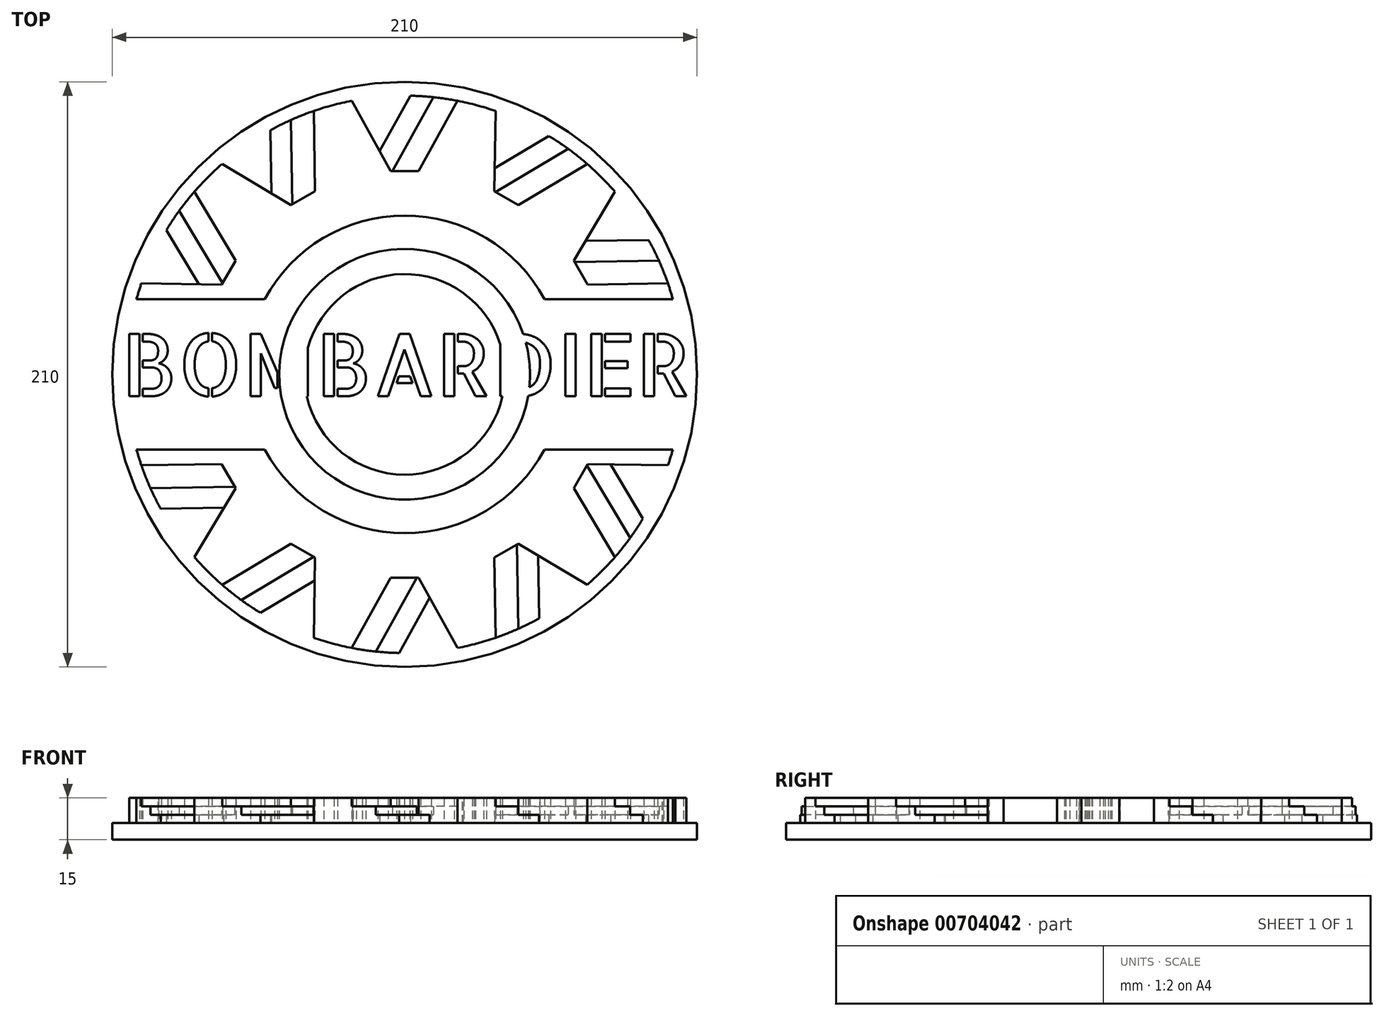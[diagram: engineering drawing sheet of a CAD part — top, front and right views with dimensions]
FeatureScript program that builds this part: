
annotation { "Feature Type Name" : "Feature", "Feature Type Description" : "" }
export const myFeature = defineFeature(function(context is Context, id is Id, definition is map)
    precondition{}
    {
        {
            var Q0;
            Q0=qCreatedBy(makeId("Top.planeOp"),FACE);
            var sketch = newSketch(context, id + "F0", { "sketchPlane" : qUnion([Q0])});
            skCircle(sketch, "E0", {"center": v(0, 0) * mm, "radius": 105 * mm});
            skSolve(sketch);
        }
        {
            var Q0;
            Q0=makeQuery(id+"F0.imprint","IMPRINT",FACE,{"disambiguationData":[TD([[makeQuery(id+"F0.imprint","IMPRINT",EDGE,{"derivedFrom":sQuery(id+"F0.wireOp",EDGE,"E0")}),1.0]])]});
            extrude(context, id + "F1", {"entities" : qUnion([Q0]), "depth" : 6 * mm, "offsetDistance" : 25 * mm});
        }
        {
            var Q0;
            Q0=makeQuery(id+"F1.opExtrude","CAP_FACE",FACE,{"disambiguationData":[OSD([sQuery(id+"F0.wireOp",EDGE,"E0")])],"isStart":false});
            var sketch = newSketch(context, id + "F2", { "sketchPlane" : qUnion([Q0])});
            skCircle(sketch, "E1", {"center": v(0, 0) * mm, "radius": 100 * mm});
            skCircle(sketch, "E2", {"center": v(0, 0) * mm, "radius": 57 * mm});
            skLineSegment(sketch, "E3", {"start": v(0, 98.18) * mm, "end": v(-19, 98.18) * mm});
            skLineSegment(sketch, "E4", {"start": v(-19, 98.18) * mm, "end": v(-5, 73) * mm});
            skLineSegment(sketch, "E5", {"start": v(-5, 73) * mm, "end": v(0, 73) * mm});
            skLineSegment(sketch, "E6.MirrorCS", {"start": v(5, 73) * mm, "end": v(0, 73) * mm});
            skLineSegment(sketch, "E7.MirrorCS", {"start": v(19, 98.18) * mm, "end": v(5, 73) * mm});
            skLineSegment(sketch, "E8.MirrorCS", {"start": v(0, 98.18) * mm, "end": v(19, 98.18) * mm});
            skLineSegment(sketch, "E9.1.0", {"start": v(-49.09, 85.02) * mm, "end": v(-65.54, 75.52) * mm});
            skLineSegment(sketch, "E9.1.1", {"start": v(-49.09, 85.02) * mm, "end": v(-32.63, 94.52) * mm});
            skLineSegment(sketch, "E9.1.2", {"start": v(-32.63, 94.52) * mm, "end": v(-32.17, 65.72) * mm});
            skLineSegment(sketch, "E9.1.3", {"start": v(-32.17, 65.72) * mm, "end": v(-36.5, 63.22) * mm});
            skLineSegment(sketch, "E9.1.4", {"start": v(-40.83, 60.72) * mm, "end": v(-36.5, 63.22) * mm});
            skLineSegment(sketch, "E9.1.5", {"start": v(-65.54, 75.52) * mm, "end": v(-40.83, 60.72) * mm});
            skLineSegment(sketch, "E9.2.0", {"start": v(-85.02, 49.09) * mm, "end": v(-94.52, 32.63) * mm});
            skLineSegment(sketch, "E9.2.1", {"start": v(-85.02, 49.09) * mm, "end": v(-75.52, 65.54) * mm});
            skLineSegment(sketch, "E9.2.2", {"start": v(-75.52, 65.54) * mm, "end": v(-60.72, 40.83) * mm});
            skLineSegment(sketch, "E9.2.3", {"start": v(-60.72, 40.83) * mm, "end": v(-63.22, 36.5) * mm});
            skLineSegment(sketch, "E9.2.4", {"start": v(-65.72, 32.17) * mm, "end": v(-63.22, 36.5) * mm});
            skLineSegment(sketch, "E9.2.5", {"start": v(-94.52, 32.63) * mm, "end": v(-65.72, 32.17) * mm});
            skLineSegment(sketch, "E9.3.0", {"start": v(-98.18, 0) * mm, "end": v(-98.18, -19) * mm});
            skLineSegment(sketch, "E9.3.1", {"start": v(-98.18, 0) * mm, "end": v(-98.18, 19) * mm});
            skLineSegment(sketch, "E9.3.2", {"start": v(-98.18, 19) * mm, "end": v(-73, 5) * mm});
            skLineSegment(sketch, "E9.3.3", {"start": v(-73, 5) * mm, "end": v(-73, 0) * mm});
            skLineSegment(sketch, "E9.3.4", {"start": v(-73, -5) * mm, "end": v(-73, 0) * mm});
            skLineSegment(sketch, "E9.3.5", {"start": v(-98.18, -19) * mm, "end": v(-73, -5) * mm});
            skLineSegment(sketch, "E9.4.0", {"start": v(-85.02, -49.09) * mm, "end": v(-75.52, -65.54) * mm});
            skLineSegment(sketch, "E9.4.1", {"start": v(-85.02, -49.09) * mm, "end": v(-94.52, -32.63) * mm});
            skLineSegment(sketch, "E9.4.2", {"start": v(-94.52, -32.63) * mm, "end": v(-65.72, -32.17) * mm});
            skLineSegment(sketch, "E9.4.3", {"start": v(-65.72, -32.17) * mm, "end": v(-63.22, -36.5) * mm});
            skLineSegment(sketch, "E9.4.4", {"start": v(-60.72, -40.83) * mm, "end": v(-63.22, -36.5) * mm});
            skLineSegment(sketch, "E9.4.5", {"start": v(-75.52, -65.54) * mm, "end": v(-60.72, -40.83) * mm});
            skLineSegment(sketch, "E9.5.0", {"start": v(-49.09, -85.02) * mm, "end": v(-32.63, -94.52) * mm});
            skLineSegment(sketch, "E9.5.1", {"start": v(-49.09, -85.02) * mm, "end": v(-65.54, -75.52) * mm});
            skLineSegment(sketch, "E9.5.2", {"start": v(-65.54, -75.52) * mm, "end": v(-40.83, -60.72) * mm});
            skLineSegment(sketch, "E9.5.3", {"start": v(-40.83, -60.72) * mm, "end": v(-36.5, -63.22) * mm});
            skLineSegment(sketch, "E9.5.4", {"start": v(-32.17, -65.72) * mm, "end": v(-36.5, -63.22) * mm});
            skLineSegment(sketch, "E9.5.5", {"start": v(-32.63, -94.52) * mm, "end": v(-32.17, -65.72) * mm});
            skLineSegment(sketch, "E9.6.0", {"start": v(0, -98.18) * mm, "end": v(19, -98.18) * mm});
            skLineSegment(sketch, "E9.6.1", {"start": v(0, -98.18) * mm, "end": v(-19, -98.18) * mm});
            skLineSegment(sketch, "E9.6.2", {"start": v(-19, -98.18) * mm, "end": v(-5, -73) * mm});
            skLineSegment(sketch, "E9.6.3", {"start": v(-5, -73) * mm, "end": v(0, -73) * mm});
            skLineSegment(sketch, "E9.6.4", {"start": v(5, -73) * mm, "end": v(0, -73) * mm});
            skLineSegment(sketch, "E9.6.5", {"start": v(19, -98.18) * mm, "end": v(5, -73) * mm});
            skLineSegment(sketch, "E9.7.0", {"start": v(49.09, -85.02) * mm, "end": v(65.54, -75.52) * mm});
            skLineSegment(sketch, "E9.7.1", {"start": v(49.09, -85.02) * mm, "end": v(32.63, -94.52) * mm});
            skLineSegment(sketch, "E9.7.2", {"start": v(32.63, -94.52) * mm, "end": v(32.17, -65.72) * mm});
            skLineSegment(sketch, "E9.7.3", {"start": v(32.17, -65.72) * mm, "end": v(36.5, -63.22) * mm});
            skLineSegment(sketch, "E9.7.4", {"start": v(40.83, -60.72) * mm, "end": v(36.5, -63.22) * mm});
            skLineSegment(sketch, "E9.7.5", {"start": v(65.54, -75.52) * mm, "end": v(40.83, -60.72) * mm});
            skLineSegment(sketch, "E9.8.0", {"start": v(85.02, -49.09) * mm, "end": v(94.52, -32.63) * mm});
            skLineSegment(sketch, "E9.8.1", {"start": v(85.02, -49.09) * mm, "end": v(75.52, -65.54) * mm});
            skLineSegment(sketch, "E9.8.2", {"start": v(75.52, -65.54) * mm, "end": v(60.72, -40.83) * mm});
            skLineSegment(sketch, "E9.8.3", {"start": v(60.72, -40.83) * mm, "end": v(63.22, -36.5) * mm});
            skLineSegment(sketch, "E9.8.4", {"start": v(65.72, -32.17) * mm, "end": v(63.22, -36.5) * mm});
            skLineSegment(sketch, "E9.8.5", {"start": v(94.52, -32.63) * mm, "end": v(65.72, -32.17) * mm});
            skLineSegment(sketch, "E9.9.0", {"start": v(98.18, 0) * mm, "end": v(98.18, 19) * mm});
            skLineSegment(sketch, "E9.9.1", {"start": v(98.18, 0) * mm, "end": v(98.18, -19) * mm});
            skLineSegment(sketch, "E9.9.2", {"start": v(98.18, -19) * mm, "end": v(73, -5) * mm});
            skLineSegment(sketch, "E9.9.3", {"start": v(73, -5) * mm, "end": v(73, 0) * mm});
            skLineSegment(sketch, "E9.9.4", {"start": v(73, 5) * mm, "end": v(73, 0) * mm});
            skLineSegment(sketch, "E9.9.5", {"start": v(98.18, 19) * mm, "end": v(73, 5) * mm});
            skLineSegment(sketch, "E9.10.0", {"start": v(85.02, 49.09) * mm, "end": v(75.52, 65.54) * mm});
            skLineSegment(sketch, "E9.10.1", {"start": v(85.02, 49.09) * mm, "end": v(94.52, 32.63) * mm});
            skLineSegment(sketch, "E9.10.2", {"start": v(94.52, 32.63) * mm, "end": v(65.72, 32.17) * mm});
            skLineSegment(sketch, "E9.10.3", {"start": v(65.72, 32.17) * mm, "end": v(63.22, 36.5) * mm});
            skLineSegment(sketch, "E9.10.4", {"start": v(60.72, 40.83) * mm, "end": v(63.22, 36.5) * mm});
            skLineSegment(sketch, "E9.10.5", {"start": v(75.52, 65.54) * mm, "end": v(60.72, 40.83) * mm});
            skLineSegment(sketch, "E9.11.0", {"start": v(49.09, 85.02) * mm, "end": v(32.63, 94.52) * mm});
            skLineSegment(sketch, "E9.11.1", {"start": v(49.09, 85.02) * mm, "end": v(65.54, 75.52) * mm});
            skLineSegment(sketch, "E9.11.2", {"start": v(65.54, 75.52) * mm, "end": v(40.83, 60.72) * mm});
            skLineSegment(sketch, "E9.11.3", {"start": v(40.83, 60.72) * mm, "end": v(36.5, 63.22) * mm});
            skLineSegment(sketch, "E9.11.4", {"start": v(32.17, 65.72) * mm, "end": v(36.5, 63.22) * mm});
            skLineSegment(sketch, "E9.11.5", {"start": v(32.63, 94.52) * mm, "end": v(32.17, 65.72) * mm});
            skCircle(sketch, "E10", {"center": v(0, 0) * mm, "radius": 45 * mm});
            skCircle(sketch, "E11", {"center": v(0, 0) * mm, "radius": 36 * mm});
            skLineSegment(sketch, "E12", {"start": v(13, 99.15) * mm, "end": v(-1.54, 73) * mm});
            skLineSegment(sketch, "E13", {"start": v(-4.4, 73) * mm, "end": v(10.31, 99.47) * mm});
            skLineSegment(sketch, "E14", {"start": v(4.83, 99.88) * mm, "end": v(-7.56, 77.6) * mm});
            skLineSegment(sketch, "E15", {"start": v(2.02, 99.98) * mm, "end": v(-9, 80.18) * mm});
            skLineSegment(sketch, "E16.1.0", {"start": v(-38.32, 92.37) * mm, "end": v(-37.83, 62.45) * mm});
            skLineSegment(sketch, "E16.1.1", {"start": v(-40.31, 61.02) * mm, "end": v(-40.8, 91.3) * mm});
            skLineSegment(sketch, "E16.1.2", {"start": v(-45.76, 88.91) * mm, "end": v(-45.35, 63.43) * mm});
            skLineSegment(sketch, "E16.1.3", {"start": v(-48.24, 87.6) * mm, "end": v(-47.88, 64.94) * mm});
            skLineSegment(sketch, "E16.2.0", {"start": v(-79.37, 60.83) * mm, "end": v(-64, 35.17) * mm});
            skLineSegment(sketch, "E16.2.1", {"start": v(-65.42, 32.69) * mm, "end": v(-80.98, 58.67) * mm});
            skLineSegment(sketch, "E16.2.2", {"start": v(-84.09, 54.12) * mm, "end": v(-70.99, 32.25) * mm});
            skLineSegment(sketch, "E16.2.3", {"start": v(-85.58, 51.74) * mm, "end": v(-73.93, 32.3) * mm});
            skLineSegment(sketch, "E16.3.0", {"start": v(-99.15, 13) * mm, "end": v(-73, -1.54) * mm});
            skLineSegment(sketch, "E16.3.1", {"start": v(-73, -4.4) * mm, "end": v(-99.47, 10.31) * mm});
            skLineSegment(sketch, "E16.3.2", {"start": v(-99.88, 4.83) * mm, "end": v(-77.6, -7.56) * mm});
            skLineSegment(sketch, "E16.3.3", {"start": v(-99.98, 2.02) * mm, "end": v(-80.18, -9) * mm});
            skLineSegment(sketch, "E16.4.0", {"start": v(-92.37, -38.32) * mm, "end": v(-62.45, -37.83) * mm});
            skLineSegment(sketch, "E16.4.1", {"start": v(-61.02, -40.31) * mm, "end": v(-91.3, -40.8) * mm});
            skLineSegment(sketch, "E16.4.2", {"start": v(-88.91, -45.76) * mm, "end": v(-63.43, -45.35) * mm});
            skLineSegment(sketch, "E16.4.3", {"start": v(-87.6, -48.24) * mm, "end": v(-64.94, -47.88) * mm});
            skLineSegment(sketch, "E16.5.0", {"start": v(-60.83, -79.37) * mm, "end": v(-35.17, -64) * mm});
            skLineSegment(sketch, "E16.5.1", {"start": v(-32.69, -65.42) * mm, "end": v(-58.67, -80.98) * mm});
            skLineSegment(sketch, "E16.5.2", {"start": v(-54.12, -84.09) * mm, "end": v(-32.25, -70.99) * mm});
            skLineSegment(sketch, "E16.5.3", {"start": v(-51.74, -85.58) * mm, "end": v(-32.3, -73.93) * mm});
            skLineSegment(sketch, "E16.6.0", {"start": v(-13, -99.15) * mm, "end": v(1.54, -73) * mm});
            skLineSegment(sketch, "E16.6.1", {"start": v(4.4, -73) * mm, "end": v(-10.31, -99.47) * mm});
            skLineSegment(sketch, "E16.6.2", {"start": v(-4.83, -99.88) * mm, "end": v(7.56, -77.6) * mm});
            skLineSegment(sketch, "E16.6.3", {"start": v(-2.02, -99.98) * mm, "end": v(9, -80.18) * mm});
            skLineSegment(sketch, "E16.7.0", {"start": v(38.32, -92.37) * mm, "end": v(37.83, -62.45) * mm});
            skLineSegment(sketch, "E16.7.1", {"start": v(40.31, -61.02) * mm, "end": v(40.8, -91.3) * mm});
            skLineSegment(sketch, "E16.7.2", {"start": v(45.76, -88.91) * mm, "end": v(45.35, -63.43) * mm});
            skLineSegment(sketch, "E16.7.3", {"start": v(48.24, -87.6) * mm, "end": v(47.88, -64.94) * mm});
            skLineSegment(sketch, "E16.8.0", {"start": v(79.37, -60.83) * mm, "end": v(64, -35.17) * mm});
            skLineSegment(sketch, "E16.8.1", {"start": v(65.42, -32.69) * mm, "end": v(80.98, -58.67) * mm});
            skLineSegment(sketch, "E16.8.2", {"start": v(84.09, -54.12) * mm, "end": v(70.99, -32.25) * mm});
            skLineSegment(sketch, "E16.8.3", {"start": v(85.58, -51.74) * mm, "end": v(73.93, -32.3) * mm});
            skLineSegment(sketch, "E16.9.0", {"start": v(99.15, -13) * mm, "end": v(73, 1.54) * mm});
            skLineSegment(sketch, "E16.9.1", {"start": v(73, 4.4) * mm, "end": v(99.47, -10.31) * mm});
            skLineSegment(sketch, "E16.9.2", {"start": v(99.88, -4.83) * mm, "end": v(77.6, 7.56) * mm});
            skLineSegment(sketch, "E16.9.3", {"start": v(99.98, -2.02) * mm, "end": v(80.18, 9) * mm});
            skLineSegment(sketch, "E16.10.0", {"start": v(92.37, 38.32) * mm, "end": v(62.45, 37.83) * mm});
            skLineSegment(sketch, "E16.10.1", {"start": v(61.02, 40.31) * mm, "end": v(91.3, 40.8) * mm});
            skLineSegment(sketch, "E16.10.2", {"start": v(88.91, 45.76) * mm, "end": v(63.43, 45.35) * mm});
            skLineSegment(sketch, "E16.10.3", {"start": v(87.6, 48.24) * mm, "end": v(64.94, 47.88) * mm});
            skLineSegment(sketch, "E16.11.0", {"start": v(60.83, 79.37) * mm, "end": v(35.17, 64) * mm});
            skLineSegment(sketch, "E16.11.1", {"start": v(32.69, 65.42) * mm, "end": v(58.67, 80.98) * mm});
            skLineSegment(sketch, "E16.11.2", {"start": v(54.12, 84.09) * mm, "end": v(32.25, 70.99) * mm});
            skLineSegment(sketch, "E16.11.3", {"start": v(51.74, 85.58) * mm, "end": v(32.3, 73.93) * mm});
            skSolve(sketch);
        }
        {
            var Q0;
            Q0=makeQuery(id+"F2.imprint","IMPRINT",FACE,{"disambiguationData":[TD([[makeQuery(id+"F2.imprint","IMPRINT",EDGE,{"derivedFrom":sQuery(id+"F2.wireOp",EDGE,"E2")}),-1.0]])]});
            var Q1;
            Q1=makeQuery(id+"F2.imprint","IMPRINT",FACE,{"disambiguationData":[TD([[makeQuery(id+"F2.imprint","IMPRINT",EDGE,{"derivedFrom":sQuery(id+"F2.wireOp",EDGE,"E10")}),1.0]])]});
            extrude(context, id + "F3", {"entities" : qUnion([Q0, Q1]), "operationType" : NewBodyOperationType.ADD, "depth" : 9 * mm, "offsetDistance" : 25 * mm});
        }
        {
            var Q0;
            Q0=makeQuery(id+"F3.boolean.opBoolean","SPLIT",FACE,{"disambiguationData":[TD([makeQuery(id+"F3.opExtrude","SWEPT_FACE",FACE,{"disambiguationData":[OSD([sQuery(id+"F2.wireOp",EDGE,"E2")])]})])],"derivedFrom":makeQuery(id+"F1.opExtrude","CAP_FACE",FACE,{"disambiguationData":[OSD([sQuery(id+"F0.wireOp",EDGE,"E0")])],"isStart":false})});
            var sketch = newSketch(context, id + "F4", { "sketchPlane" : qUnion([Q0])});
            skLineSegment(sketch, "E17.bottom", {"start": v(-113.63, 27) * mm, "end": v(113.63, 27) * mm});
            skLineSegment(sketch, "E17.top", {"start": v(-113.63, -27) * mm, "end": v(113.63, -27) * mm});
            skLineSegment(sketch, "E17.left", {"start": v(-113.63, 27) * mm, "end": v(-113.63, -27) * mm});
            skLineSegment(sketch, "E17.right", {"start": v(113.63, 27) * mm, "end": v(113.63, -27) * mm});
            skPoint(sketch, "E17.middle", {"position": v(0, 0) * mm});
            skSolve(sketch);
        }
        {
            var Q0;
            {var subQ0=sQuery(id+"F4.wireOp",EDGE,"E17.left");Q0=makeQuery(id+"F4.imprint","IMPRINT",FACE,{"disambiguationData":[TD([[makeQuery(id+"F4.imprint","IMPRINT",EDGE,{"derivedFrom":subQ0}),1.0]])]});}
            var Q1;
            {var subQ0=sQuery(id+"F4.wireOp",EDGE,"E17.bottom");var subQ1=makeQuery(id+"F3.opExtrude","CAP_EDGE",EDGE,{"disambiguationData":[OSD([sQuery(id+"F2.wireOp",EDGE,"E10")])],"isStart":true});var subQ2=makeQuery(id+"F4.imprint","INTERSECT",VERTEX,{"disambiguationData":[OD(0.0)],"derivedFrom":[subQ1,subQ0]});Q1=makeQuery(id+"F4.imprint","IMPRINT",FACE,{"disambiguationData":[TD([[makeQuery(id+"F4.imprint","IMPRINT",EDGE,{"disambiguationData":[TD([[subQ2,-1.0]])],"derivedFrom":subQ0}),-1.0]])]});}
            var Q2;
            {var subQ0=sQuery(id+"F4.wireOp",EDGE,"E17.right");Q2=makeQuery(id+"F4.imprint","IMPRINT",FACE,{"disambiguationData":[TD([[makeQuery(id+"F4.imprint","IMPRINT",EDGE,{"derivedFrom":subQ0}),-1.0]])]});}
            extrude(context, id + "F5", {"entities" : qUnion([Q0, Q1, Q2]), "operationType" : NewBodyOperationType.REMOVE, "depth" : 52.9 * mm, "offsetDistance" : 25 * mm});
        }
        {
            var Q0;
            {var subQ0=sQuery(id+"F4.wireOp",EDGE,"E17.top");var subQ1=sQuery(id+"F4.wireOp",EDGE,"E17.bottom");var subQ2=sQuery(id+"F2.wireOp",EDGE,"E2");var subQ3=sQuery(id+"F2.wireOp",EDGE,"E10");var subQ4=sQuery(id+"F0.wireOp",EDGE,"E0");var subQ5=makeQuery(id+"F1.opExtrude","CAP_FACE",FACE,{"disambiguationData":[OSD([subQ4])],"isStart":false});Q0=makeQuery(id+"F5.boolean.opBoolean","MERGE",FACE,{"derivedFrom":[makeQuery(id+"F3.boolean.opBoolean","SPLIT",FACE,{"disambiguationData":[TD([makeQuery(id+"F1.opExtrude","SWEPT_FACE",FACE,{"disambiguationData":[OSD([subQ4])]})])],"derivedFrom":subQ5}),makeQuery(id+"F3.boolean.opBoolean","SPLIT",FACE,{"disambiguationData":[TD([makeQuery(id+"F3.opExtrude","SWEPT_FACE",FACE,{"disambiguationData":[OSD([subQ2])]})])],"derivedFrom":subQ5}),makeQuery(id+"F3.boolean.opBoolean","SPLIT",FACE,{"disambiguationData":[TD([makeQuery(id+"F3.opExtrude","SWEPT_FACE",FACE,{"disambiguationData":[OSD([sQuery(id+"F2.wireOp",EDGE,"E11")])]})])],"derivedFrom":subQ5}),makeQuery(id+"F5.opExtrude","CAP_FACE",FACE,{"disambiguationData":[OSD([subQ2,subQ1,subQ0,sQuery(id+"F4.wireOp",EDGE,"E17.left")])],"isStart":true}),makeQuery(id+"F5.opExtrude","CAP_FACE",FACE,{"disambiguationData":[OSD([subQ3,subQ1,subQ0])],"isStart":true}),makeQuery(id+"F5.opExtrude","CAP_FACE",FACE,{"disambiguationData":[OSD([subQ2,subQ1,subQ0,sQuery(id+"F4.wireOp",EDGE,"E17.right")])],"isStart":true})]});}
            var sketch = newSketch(context, id + "F6", { "sketchPlane" : qUnion([Q0])});
            skText(sketch, "E18", { "text": "BOMBARDIER", "fontName": "AllertaStencil-Regular.ttf"});
            const initialGuessF6  = {"E18": [-0.1018, -0.00782, 1, 0, 0.02236]};
            skSetInitialGuess(sketch, initialGuessF6);
            skSolve(sketch);
        }
        {
            var Q0;
            Q0 = qSketchRegion(id + "F6", true);
            extrude(context, id + "F7", {"entities" : qUnion([Q0]), "operationType" : NewBodyOperationType.ADD, "depth" : 9 * mm, "offsetDistance" : 25 * mm});
        }
        {
            var Q0;
            {var subQ0=sQuery(id+"F2.wireOp",EDGE,"E14");var subQ1=sQuery(id+"F2.wireOp",EDGE,"E1");var subQ2=makeQuery(id+"F2.imprint","INTERSECT",VERTEX,{"derivedFrom":[subQ1,subQ0]});Q0=makeQuery(id+"F2.imprint","IMPRINT",FACE,{"disambiguationData":[TD([[makeQuery(id+"F2.imprint","IMPRINT",EDGE,{"disambiguationData":[TD([[subQ2,-1.0]])],"derivedFrom":subQ1}),1.0]])]});}
            var Q1;
            {var subQ0=sQuery(id+"F2.wireOp",EDGE,"E14");var subQ1=sQuery(id+"F2.wireOp",EDGE,"E4");var subQ2=makeQuery(id+"F2.imprint","INTERSECT",VERTEX,{"derivedFrom":[subQ1,subQ0]});Q1=makeQuery(id+"F2.imprint","IMPRINT",FACE,{"disambiguationData":[TD([[makeQuery(id+"F2.imprint","IMPRINT",EDGE,{"disambiguationData":[TD([[subQ2,1.0]])],"derivedFrom":subQ1}),1.0]])]});}
            var Q2;
            {var subQ1=sQuery(id+"F2.wireOp",EDGE,"E5");var subQ7=sQuery(id+"F2.wireOp",EDGE,"E4");var subQ8=makeQuery(id+"F2.imprint","INTERSECT",VERTEX,{"derivedFrom":[subQ7,subQ1]});Q2=makeQuery(id+"F2.imprint","IMPRINT",FACE,{"disambiguationData":[TD([[makeQuery(id+"F2.imprint","IMPRINT",EDGE,{"disambiguationData":[TD([[subQ8,1.0]])],"derivedFrom":subQ7}),1.0]])]});}
            var Q3;
            {var subQ0=sQuery(id+"F2.wireOp",EDGE,"E13");var subQ1=sQuery(id+"F2.wireOp",EDGE,"E1");var subQ2=makeQuery(id+"F2.imprint","INTERSECT",VERTEX,{"derivedFrom":[subQ1,subQ0]});Q3=makeQuery(id+"F2.imprint","IMPRINT",FACE,{"disambiguationData":[TD([[makeQuery(id+"F2.imprint","IMPRINT",EDGE,{"disambiguationData":[TD([[subQ2,-1.0]])],"derivedFrom":subQ1}),1.0]])]});}
            var Q4;
            {var subQ0=sQuery(id+"F2.wireOp",EDGE,"E16.11.2");var subQ1=sQuery(id+"F2.wireOp",EDGE,"E1");var subQ2=makeQuery(id+"F2.imprint","INTERSECT",VERTEX,{"derivedFrom":[subQ1,subQ0]});Q4=makeQuery(id+"F2.imprint","IMPRINT",FACE,{"disambiguationData":[TD([[makeQuery(id+"F2.imprint","IMPRINT",EDGE,{"disambiguationData":[TD([[subQ2,-1.0]])],"derivedFrom":subQ1}),1.0]])]});}
            var Q5;
            {var subQ0=sQuery(id+"F2.wireOp",EDGE,"E16.11.3");var subQ1=sQuery(id+"F2.wireOp",EDGE,"E9.11.1");var subQ2=makeQuery(id+"F2.imprint","INTERSECT",VERTEX,{"derivedFrom":[subQ1,subQ0]});Q5=makeQuery(id+"F2.imprint","IMPRINT",FACE,{"disambiguationData":[TD([[makeQuery(id+"F2.imprint","IMPRINT",EDGE,{"disambiguationData":[TD([[subQ2,-1.0]])],"derivedFrom":subQ1}),-1.0]])]});}
            var Q6;
            {var subQ3=sQuery(id+"F2.wireOp",EDGE,"E9.11.1");var subQ7=sQuery(id+"F2.wireOp",EDGE,"E16.11.2");var subQ9=makeQuery(id+"F2.imprint","INTERSECT",VERTEX,{"derivedFrom":[subQ3,subQ7]});Q6=makeQuery(id+"F2.imprint","IMPRINT",FACE,{"disambiguationData":[TD([[makeQuery(id+"F2.imprint","IMPRINT",EDGE,{"disambiguationData":[TD([[subQ9,-1.0]])],"derivedFrom":subQ3}),-1.0]])]});}
            var Q7;
            {var subQ0=sQuery(id+"F2.wireOp",EDGE,"E16.11.1");var subQ1=sQuery(id+"F2.wireOp",EDGE,"E1");var subQ2=makeQuery(id+"F2.imprint","INTERSECT",VERTEX,{"derivedFrom":[subQ1,subQ0]});Q7=makeQuery(id+"F2.imprint","IMPRINT",FACE,{"disambiguationData":[TD([[makeQuery(id+"F2.imprint","IMPRINT",EDGE,{"disambiguationData":[TD([[subQ2,-1.0]])],"derivedFrom":subQ1}),1.0]])]});}
            var Q8;
            {var subQ0=sQuery(id+"F2.wireOp",EDGE,"E16.10.3");var subQ1=sQuery(id+"F2.wireOp",EDGE,"E9.10.1");var subQ2=makeQuery(id+"F2.imprint","INTERSECT",VERTEX,{"derivedFrom":[subQ1,subQ0]});Q8=makeQuery(id+"F2.imprint","IMPRINT",FACE,{"disambiguationData":[TD([[makeQuery(id+"F2.imprint","IMPRINT",EDGE,{"disambiguationData":[TD([[subQ2,-1.0]])],"derivedFrom":subQ1}),-1.0]])]});}
            var Q9;
            {var subQ0=sQuery(id+"F2.wireOp",EDGE,"E16.10.2");var subQ1=sQuery(id+"F2.wireOp",EDGE,"E1");var subQ2=makeQuery(id+"F2.imprint","INTERSECT",VERTEX,{"derivedFrom":[subQ1,subQ0]});Q9=makeQuery(id+"F2.imprint","IMPRINT",FACE,{"disambiguationData":[TD([[makeQuery(id+"F2.imprint","IMPRINT",EDGE,{"disambiguationData":[TD([[subQ2,-1.0]])],"derivedFrom":subQ1}),1.0]])]});}
            var Q10;
            {var subQ0=sQuery(id+"F2.wireOp",EDGE,"E16.10.1");var subQ1=sQuery(id+"F2.wireOp",EDGE,"E1");var subQ2=makeQuery(id+"F2.imprint","INTERSECT",VERTEX,{"derivedFrom":[subQ1,subQ0]});Q10=makeQuery(id+"F2.imprint","IMPRINT",FACE,{"disambiguationData":[TD([[makeQuery(id+"F2.imprint","IMPRINT",EDGE,{"disambiguationData":[TD([[subQ2,-1.0]])],"derivedFrom":subQ1}),1.0]])]});}
            var Q11;
            {var subQ3=sQuery(id+"F2.wireOp",EDGE,"E9.10.1");var subQ7=sQuery(id+"F2.wireOp",EDGE,"E16.10.2");var subQ9=makeQuery(id+"F2.imprint","INTERSECT",VERTEX,{"derivedFrom":[subQ3,subQ7]});Q11=makeQuery(id+"F2.imprint","IMPRINT",FACE,{"disambiguationData":[TD([[makeQuery(id+"F2.imprint","IMPRINT",EDGE,{"disambiguationData":[TD([[subQ9,-1.0]])],"derivedFrom":subQ3}),-1.0]])]});}
            var Q12;
            {var subQ0=sQuery(id+"F2.wireOp",EDGE,"E16.8.3");var subQ1=sQuery(id+"F2.wireOp",EDGE,"E9.8.1");var subQ2=makeQuery(id+"F2.imprint","INTERSECT",VERTEX,{"derivedFrom":[subQ1,subQ0]});Q12=makeQuery(id+"F2.imprint","IMPRINT",FACE,{"disambiguationData":[TD([[makeQuery(id+"F2.imprint","IMPRINT",EDGE,{"disambiguationData":[TD([[subQ2,-1.0]])],"derivedFrom":subQ1}),-1.0]])]});}
            var Q13;
            {var subQ3=sQuery(id+"F2.wireOp",EDGE,"E9.8.1");var subQ5=sQuery(id+"F2.wireOp",EDGE,"E16.8.2");var subQ6=makeQuery(id+"F2.imprint","INTERSECT",VERTEX,{"derivedFrom":[subQ3,subQ5]});Q13=makeQuery(id+"F2.imprint","IMPRINT",FACE,{"disambiguationData":[TD([[makeQuery(id+"F2.imprint","IMPRINT",EDGE,{"disambiguationData":[TD([[subQ6,-1.0]])],"derivedFrom":subQ3}),-1.0]])]});}
            var Q14;
            {var subQ0=sQuery(id+"F2.wireOp",EDGE,"E16.8.2");var subQ1=sQuery(id+"F2.wireOp",EDGE,"E1");var subQ2=makeQuery(id+"F2.imprint","INTERSECT",VERTEX,{"derivedFrom":[subQ1,subQ0]});Q14=makeQuery(id+"F2.imprint","IMPRINT",FACE,{"disambiguationData":[TD([[makeQuery(id+"F2.imprint","IMPRINT",EDGE,{"disambiguationData":[TD([[subQ2,-1.0]])],"derivedFrom":subQ1}),1.0]])]});}
            var Q15;
            {var subQ0=sQuery(id+"F2.wireOp",EDGE,"E16.8.1");var subQ1=sQuery(id+"F2.wireOp",EDGE,"E1");var subQ2=makeQuery(id+"F2.imprint","INTERSECT",VERTEX,{"derivedFrom":[subQ1,subQ0]});Q15=makeQuery(id+"F2.imprint","IMPRINT",FACE,{"disambiguationData":[TD([[makeQuery(id+"F2.imprint","IMPRINT",EDGE,{"disambiguationData":[TD([[subQ2,-1.0]])],"derivedFrom":subQ1}),1.0]])]});}
            var Q16;
            {var subQ0=sQuery(id+"F2.wireOp",EDGE,"E16.7.3");var subQ1=sQuery(id+"F2.wireOp",EDGE,"E9.7.1");var subQ2=makeQuery(id+"F2.imprint","INTERSECT",VERTEX,{"derivedFrom":[subQ1,subQ0]});Q16=makeQuery(id+"F2.imprint","IMPRINT",FACE,{"disambiguationData":[TD([[makeQuery(id+"F2.imprint","IMPRINT",EDGE,{"disambiguationData":[TD([[subQ2,-1.0]])],"derivedFrom":subQ1}),-1.0]])]});}
            var Q17;
            {var subQ3=sQuery(id+"F2.wireOp",EDGE,"E9.7.1");var subQ7=sQuery(id+"F2.wireOp",EDGE,"E16.7.2");var subQ9=makeQuery(id+"F2.imprint","INTERSECT",VERTEX,{"derivedFrom":[subQ3,subQ7]});Q17=makeQuery(id+"F2.imprint","IMPRINT",FACE,{"disambiguationData":[TD([[makeQuery(id+"F2.imprint","IMPRINT",EDGE,{"disambiguationData":[TD([[subQ9,-1.0]])],"derivedFrom":subQ3}),-1.0]])]});}
            var Q18;
            {var subQ0=sQuery(id+"F2.wireOp",EDGE,"E16.7.1");var subQ1=sQuery(id+"F2.wireOp",EDGE,"E1");var subQ2=makeQuery(id+"F2.imprint","INTERSECT",VERTEX,{"derivedFrom":[subQ1,subQ0]});Q18=makeQuery(id+"F2.imprint","IMPRINT",FACE,{"disambiguationData":[TD([[makeQuery(id+"F2.imprint","IMPRINT",EDGE,{"disambiguationData":[TD([[subQ2,-1.0]])],"derivedFrom":subQ1}),1.0]])]});}
            var Q19;
            {var subQ0=sQuery(id+"F2.wireOp",EDGE,"E16.7.2");var subQ1=sQuery(id+"F2.wireOp",EDGE,"E1");var subQ2=makeQuery(id+"F2.imprint","INTERSECT",VERTEX,{"derivedFrom":[subQ1,subQ0]});Q19=makeQuery(id+"F2.imprint","IMPRINT",FACE,{"disambiguationData":[TD([[makeQuery(id+"F2.imprint","IMPRINT",EDGE,{"disambiguationData":[TD([[subQ2,-1.0]])],"derivedFrom":subQ1}),1.0]])]});}
            var Q20;
            {var subQ0=sQuery(id+"F2.wireOp",EDGE,"E16.6.1");var subQ1=sQuery(id+"F2.wireOp",EDGE,"E1");var subQ2=makeQuery(id+"F2.imprint","INTERSECT",VERTEX,{"derivedFrom":[subQ1,subQ0]});Q20=makeQuery(id+"F2.imprint","IMPRINT",FACE,{"disambiguationData":[TD([[makeQuery(id+"F2.imprint","IMPRINT",EDGE,{"disambiguationData":[TD([[subQ2,-1.0]])],"derivedFrom":subQ1}),1.0]])]});}
            var Q21;
            {var subQ3=sQuery(id+"F2.wireOp",EDGE,"E9.6.1");var subQ7=sQuery(id+"F2.wireOp",EDGE,"E16.6.2");var subQ9=makeQuery(id+"F2.imprint","INTERSECT",VERTEX,{"derivedFrom":[subQ3,subQ7]});Q21=makeQuery(id+"F2.imprint","IMPRINT",FACE,{"disambiguationData":[TD([[makeQuery(id+"F2.imprint","IMPRINT",EDGE,{"disambiguationData":[TD([[subQ9,-1.0]])],"derivedFrom":subQ3}),-1.0]])]});}
            var Q22;
            {var subQ0=sQuery(id+"F2.wireOp",EDGE,"E16.6.3");var subQ1=sQuery(id+"F2.wireOp",EDGE,"E9.6.1");var subQ2=makeQuery(id+"F2.imprint","INTERSECT",VERTEX,{"derivedFrom":[subQ1,subQ0]});Q22=makeQuery(id+"F2.imprint","IMPRINT",FACE,{"disambiguationData":[TD([[makeQuery(id+"F2.imprint","IMPRINT",EDGE,{"disambiguationData":[TD([[subQ2,-1.0]])],"derivedFrom":subQ1}),-1.0]])]});}
            var Q23;
            {var subQ0=sQuery(id+"F2.wireOp",EDGE,"E16.6.2");var subQ1=sQuery(id+"F2.wireOp",EDGE,"E1");var subQ2=makeQuery(id+"F2.imprint","INTERSECT",VERTEX,{"derivedFrom":[subQ1,subQ0]});Q23=makeQuery(id+"F2.imprint","IMPRINT",FACE,{"disambiguationData":[TD([[makeQuery(id+"F2.imprint","IMPRINT",EDGE,{"disambiguationData":[TD([[subQ2,-1.0]])],"derivedFrom":subQ1}),1.0]])]});}
            var Q24;
            {var subQ0=sQuery(id+"F2.wireOp",EDGE,"E16.5.3");var subQ1=sQuery(id+"F2.wireOp",EDGE,"E9.5.1");var subQ2=makeQuery(id+"F2.imprint","INTERSECT",VERTEX,{"derivedFrom":[subQ1,subQ0]});Q24=makeQuery(id+"F2.imprint","IMPRINT",FACE,{"disambiguationData":[TD([[makeQuery(id+"F2.imprint","IMPRINT",EDGE,{"disambiguationData":[TD([[subQ2,-1.0]])],"derivedFrom":subQ1}),-1.0]])]});}
            var Q25;
            {var subQ3=sQuery(id+"F2.wireOp",EDGE,"E9.5.1");var subQ7=sQuery(id+"F2.wireOp",EDGE,"E16.5.2");var subQ9=makeQuery(id+"F2.imprint","INTERSECT",VERTEX,{"derivedFrom":[subQ3,subQ7]});Q25=makeQuery(id+"F2.imprint","IMPRINT",FACE,{"disambiguationData":[TD([[makeQuery(id+"F2.imprint","IMPRINT",EDGE,{"disambiguationData":[TD([[subQ9,-1.0]])],"derivedFrom":subQ3}),-1.0]])]});}
            var Q26;
            {var subQ0=sQuery(id+"F2.wireOp",EDGE,"E16.5.1");var subQ1=sQuery(id+"F2.wireOp",EDGE,"E1");var subQ2=makeQuery(id+"F2.imprint","INTERSECT",VERTEX,{"derivedFrom":[subQ1,subQ0]});Q26=makeQuery(id+"F2.imprint","IMPRINT",FACE,{"disambiguationData":[TD([[makeQuery(id+"F2.imprint","IMPRINT",EDGE,{"disambiguationData":[TD([[subQ2,-1.0]])],"derivedFrom":subQ1}),1.0]])]});}
            var Q27;
            {var subQ0=sQuery(id+"F2.wireOp",EDGE,"E16.5.2");var subQ1=sQuery(id+"F2.wireOp",EDGE,"E1");var subQ2=makeQuery(id+"F2.imprint","INTERSECT",VERTEX,{"derivedFrom":[subQ1,subQ0]});Q27=makeQuery(id+"F2.imprint","IMPRINT",FACE,{"disambiguationData":[TD([[makeQuery(id+"F2.imprint","IMPRINT",EDGE,{"disambiguationData":[TD([[subQ2,-1.0]])],"derivedFrom":subQ1}),1.0]])]});}
            var Q28;
            {var subQ0=sQuery(id+"F2.wireOp",EDGE,"E16.4.2");var subQ1=sQuery(id+"F2.wireOp",EDGE,"E1");var subQ2=makeQuery(id+"F2.imprint","INTERSECT",VERTEX,{"derivedFrom":[subQ1,subQ0]});Q28=makeQuery(id+"F2.imprint","IMPRINT",FACE,{"disambiguationData":[TD([[makeQuery(id+"F2.imprint","IMPRINT",EDGE,{"disambiguationData":[TD([[subQ2,-1.0]])],"derivedFrom":subQ1}),1.0]])]});}
            var Q29;
            {var subQ0=sQuery(id+"F2.wireOp",EDGE,"E16.4.3");var subQ1=sQuery(id+"F2.wireOp",EDGE,"E9.4.1");var subQ2=makeQuery(id+"F2.imprint","INTERSECT",VERTEX,{"derivedFrom":[subQ1,subQ0]});Q29=makeQuery(id+"F2.imprint","IMPRINT",FACE,{"disambiguationData":[TD([[makeQuery(id+"F2.imprint","IMPRINT",EDGE,{"disambiguationData":[TD([[subQ2,-1.0]])],"derivedFrom":subQ1}),-1.0]])]});}
            var Q30;
            {var subQ3=sQuery(id+"F2.wireOp",EDGE,"E9.4.1");var subQ7=sQuery(id+"F2.wireOp",EDGE,"E16.4.2");var subQ9=makeQuery(id+"F2.imprint","INTERSECT",VERTEX,{"derivedFrom":[subQ3,subQ7]});Q30=makeQuery(id+"F2.imprint","IMPRINT",FACE,{"disambiguationData":[TD([[makeQuery(id+"F2.imprint","IMPRINT",EDGE,{"disambiguationData":[TD([[subQ9,-1.0]])],"derivedFrom":subQ3}),-1.0]])]});}
            var Q31;
            {var subQ0=sQuery(id+"F2.wireOp",EDGE,"E16.4.1");var subQ1=sQuery(id+"F2.wireOp",EDGE,"E1");var subQ2=makeQuery(id+"F2.imprint","INTERSECT",VERTEX,{"derivedFrom":[subQ1,subQ0]});Q31=makeQuery(id+"F2.imprint","IMPRINT",FACE,{"disambiguationData":[TD([[makeQuery(id+"F2.imprint","IMPRINT",EDGE,{"disambiguationData":[TD([[subQ2,-1.0]])],"derivedFrom":subQ1}),1.0]])]});}
            var Q32;
            {var subQ0=sQuery(id+"F2.wireOp",EDGE,"E16.2.2");var subQ1=sQuery(id+"F2.wireOp",EDGE,"E1");var subQ2=makeQuery(id+"F2.imprint","INTERSECT",VERTEX,{"derivedFrom":[subQ1,subQ0]});Q32=makeQuery(id+"F2.imprint","IMPRINT",FACE,{"disambiguationData":[TD([[makeQuery(id+"F2.imprint","IMPRINT",EDGE,{"disambiguationData":[TD([[subQ2,-1.0]])],"derivedFrom":subQ1}),1.0]])]});}
            var Q33;
            {var subQ0=sQuery(id+"F2.wireOp",EDGE,"E16.2.3");var subQ1=sQuery(id+"F2.wireOp",EDGE,"E9.2.1");var subQ2=makeQuery(id+"F2.imprint","INTERSECT",VERTEX,{"derivedFrom":[subQ1,subQ0]});Q33=makeQuery(id+"F2.imprint","IMPRINT",FACE,{"disambiguationData":[TD([[makeQuery(id+"F2.imprint","IMPRINT",EDGE,{"disambiguationData":[TD([[subQ2,-1.0]])],"derivedFrom":subQ1}),-1.0]])]});}
            var Q34;
            {var subQ3=sQuery(id+"F2.wireOp",EDGE,"E9.2.1");var subQ7=sQuery(id+"F2.wireOp",EDGE,"E16.2.2");var subQ9=makeQuery(id+"F2.imprint","INTERSECT",VERTEX,{"derivedFrom":[subQ3,subQ7]});Q34=makeQuery(id+"F2.imprint","IMPRINT",FACE,{"disambiguationData":[TD([[makeQuery(id+"F2.imprint","IMPRINT",EDGE,{"disambiguationData":[TD([[subQ9,-1.0]])],"derivedFrom":subQ3}),-1.0]])]});}
            var Q35;
            {var subQ0=sQuery(id+"F2.wireOp",EDGE,"E16.2.1");var subQ1=sQuery(id+"F2.wireOp",EDGE,"E1");var subQ2=makeQuery(id+"F2.imprint","INTERSECT",VERTEX,{"derivedFrom":[subQ1,subQ0]});Q35=makeQuery(id+"F2.imprint","IMPRINT",FACE,{"disambiguationData":[TD([[makeQuery(id+"F2.imprint","IMPRINT",EDGE,{"disambiguationData":[TD([[subQ2,-1.0]])],"derivedFrom":subQ1}),1.0]])]});}
            var Q36;
            {var subQ3=sQuery(id+"F2.wireOp",EDGE,"E9.1.1");var subQ7=sQuery(id+"F2.wireOp",EDGE,"E16.1.2");var subQ9=makeQuery(id+"F2.imprint","INTERSECT",VERTEX,{"derivedFrom":[subQ3,subQ7]});Q36=makeQuery(id+"F2.imprint","IMPRINT",FACE,{"disambiguationData":[TD([[makeQuery(id+"F2.imprint","IMPRINT",EDGE,{"disambiguationData":[TD([[subQ9,-1.0]])],"derivedFrom":subQ3}),-1.0]])]});}
            var Q37;
            {var subQ0=sQuery(id+"F2.wireOp",EDGE,"E16.1.1");var subQ1=sQuery(id+"F2.wireOp",EDGE,"E1");var subQ2=makeQuery(id+"F2.imprint","INTERSECT",VERTEX,{"derivedFrom":[subQ1,subQ0]});Q37=makeQuery(id+"F2.imprint","IMPRINT",FACE,{"disambiguationData":[TD([[makeQuery(id+"F2.imprint","IMPRINT",EDGE,{"disambiguationData":[TD([[subQ2,-1.0]])],"derivedFrom":subQ1}),1.0]])]});}
            var Q38;
            {var subQ0=sQuery(id+"F2.wireOp",EDGE,"E16.1.2");var subQ1=sQuery(id+"F2.wireOp",EDGE,"E1");var subQ2=makeQuery(id+"F2.imprint","INTERSECT",VERTEX,{"derivedFrom":[subQ1,subQ0]});Q38=makeQuery(id+"F2.imprint","IMPRINT",FACE,{"disambiguationData":[TD([[makeQuery(id+"F2.imprint","IMPRINT",EDGE,{"disambiguationData":[TD([[subQ2,-1.0]])],"derivedFrom":subQ1}),1.0]])]});}
            var Q39;
            {var subQ0=sQuery(id+"F2.wireOp",EDGE,"E16.1.3");var subQ1=sQuery(id+"F2.wireOp",EDGE,"E9.1.1");var subQ2=makeQuery(id+"F2.imprint","INTERSECT",VERTEX,{"derivedFrom":[subQ1,subQ0]});Q39=makeQuery(id+"F2.imprint","IMPRINT",FACE,{"disambiguationData":[TD([[makeQuery(id+"F2.imprint","IMPRINT",EDGE,{"disambiguationData":[TD([[subQ2,-1.0]])],"derivedFrom":subQ1}),-1.0]])]});}
            extrude(context, id + "F8", {"entities" : qUnion([Q0, Q1, Q2, Q3, Q4, Q5, Q6, Q7, Q8, Q9, Q10, Q11, Q12, Q13, Q14, Q15, Q16, Q17, Q18, Q19, Q20, Q21, Q22, Q23, Q24, Q25, Q26, Q27, Q28, Q29, Q30, Q31, Q32, Q33, Q34, Q35, Q36, Q37, Q38, Q39]), "operationType" : NewBodyOperationType.ADD, "depth" : 3 * mm, "offsetDistance" : 25 * mm});
        }
        {
            var Q0;
            {var subQ0=sQuery(id+"F2.wireOp",EDGE,"E12");var subQ1=sQuery(id+"F2.wireOp",EDGE,"E5");var subQ2=makeQuery(id+"F2.imprint","INTERSECT",VERTEX,{"derivedFrom":[subQ1,subQ0]});Q0=makeQuery(id+"F2.imprint","IMPRINT",FACE,{"disambiguationData":[TD([[makeQuery(id+"F2.imprint","IMPRINT",EDGE,{"disambiguationData":[TD([[subQ2,1.0]])],"derivedFrom":subQ1}),1.0]])]});}
            var Q1;
            {var subQ4=sQuery(id+"F2.wireOp",EDGE,"E6.MirrorCS");Q1=makeQuery(id+"F2.imprint","IMPRINT",FACE,{"disambiguationData":[TD([[makeQuery(id+"F2.imprint","IMPRINT",EDGE,{"derivedFrom":subQ4}),-1.0]])]});}
            var Q2;
            {var subQ1=sQuery(id+"F2.wireOp",EDGE,"E1");var subQ3=sQuery(id+"F2.wireOp",EDGE,"E12");var subQ4=makeQuery(id+"F2.imprint","INTERSECT",VERTEX,{"derivedFrom":[subQ1,subQ3]});Q2=makeQuery(id+"F2.imprint","IMPRINT",FACE,{"disambiguationData":[TD([[makeQuery(id+"F2.imprint","IMPRINT",EDGE,{"disambiguationData":[TD([[subQ4,-1.0]])],"derivedFrom":subQ3}),1.0]])]});}
            var Q3;
            {var subQ0=sQuery(id+"F2.wireOp",EDGE,"E12");var subQ1=sQuery(id+"F2.wireOp",EDGE,"E1");var subQ2=makeQuery(id+"F2.imprint","INTERSECT",VERTEX,{"derivedFrom":[subQ1,subQ0]});Q3=makeQuery(id+"F2.imprint","IMPRINT",FACE,{"disambiguationData":[TD([[makeQuery(id+"F2.imprint","IMPRINT",EDGE,{"disambiguationData":[TD([[subQ2,-1.0]])],"derivedFrom":subQ1}),1.0]])]});}
            var Q4;
            {var subQ0=sQuery(id+"F2.wireOp",EDGE,"E16.11.0");var subQ1=sQuery(id+"F2.wireOp",EDGE,"E1");var subQ2=makeQuery(id+"F2.imprint","INTERSECT",VERTEX,{"derivedFrom":[subQ1,subQ0]});Q4=makeQuery(id+"F2.imprint","IMPRINT",FACE,{"disambiguationData":[TD([[makeQuery(id+"F2.imprint","IMPRINT",EDGE,{"disambiguationData":[TD([[subQ2,-1.0]])],"derivedFrom":subQ1}),1.0]])]});}
            var Q5;
            {var subQ1=sQuery(id+"F2.wireOp",EDGE,"E1");var subQ3=sQuery(id+"F2.wireOp",EDGE,"E16.11.0");var subQ4=makeQuery(id+"F2.imprint","INTERSECT",VERTEX,{"derivedFrom":[subQ1,subQ3]});Q5=makeQuery(id+"F2.imprint","IMPRINT",FACE,{"disambiguationData":[TD([[makeQuery(id+"F2.imprint","IMPRINT",EDGE,{"disambiguationData":[TD([[subQ4,-1.0]])],"derivedFrom":subQ3}),1.0]])]});}
            var Q6;
            {var subQ1=sQuery(id+"F2.wireOp",EDGE,"E9.11.2");Q6=makeQuery(id+"F2.imprint","IMPRINT",FACE,{"disambiguationData":[TD([[makeQuery(id+"F2.imprint","IMPRINT",EDGE,{"derivedFrom":subQ1}),-1.0]])]});}
            var Q7;
            {var subQ0=sQuery(id+"F2.wireOp",EDGE,"E16.11.1");var subQ1=sQuery(id+"F2.wireOp",EDGE,"E9.11.1");var subQ2=makeQuery(id+"F2.imprint","INTERSECT",VERTEX,{"derivedFrom":[subQ1,subQ0]});Q7=makeQuery(id+"F2.imprint","IMPRINT",FACE,{"disambiguationData":[TD([[makeQuery(id+"F2.imprint","IMPRINT",EDGE,{"disambiguationData":[TD([[subQ2,-1.0]])],"derivedFrom":subQ1}),-1.0]])]});}
            var Q8;
            {var subQ0=sQuery(id+"F2.wireOp",EDGE,"E16.10.1");var subQ1=sQuery(id+"F2.wireOp",EDGE,"E9.10.1");var subQ2=makeQuery(id+"F2.imprint","INTERSECT",VERTEX,{"derivedFrom":[subQ1,subQ0]});Q8=makeQuery(id+"F2.imprint","IMPRINT",FACE,{"disambiguationData":[TD([[makeQuery(id+"F2.imprint","IMPRINT",EDGE,{"disambiguationData":[TD([[subQ2,-1.0]])],"derivedFrom":subQ1}),-1.0]])]});}
            var Q9;
            {var subQ0=sQuery(id+"F2.wireOp",EDGE,"E16.10.0");var subQ1=sQuery(id+"F2.wireOp",EDGE,"E1");var subQ2=makeQuery(id+"F2.imprint","INTERSECT",VERTEX,{"derivedFrom":[subQ1,subQ0]});Q9=makeQuery(id+"F2.imprint","IMPRINT",FACE,{"disambiguationData":[TD([[makeQuery(id+"F2.imprint","IMPRINT",EDGE,{"disambiguationData":[TD([[subQ2,-1.0]])],"derivedFrom":subQ1}),1.0]])]});}
            var Q10;
            {var subQ1=sQuery(id+"F2.wireOp",EDGE,"E1");var subQ3=sQuery(id+"F2.wireOp",EDGE,"E16.10.0");var subQ4=makeQuery(id+"F2.imprint","INTERSECT",VERTEX,{"derivedFrom":[subQ1,subQ3]});Q10=makeQuery(id+"F2.imprint","IMPRINT",FACE,{"disambiguationData":[TD([[makeQuery(id+"F2.imprint","IMPRINT",EDGE,{"disambiguationData":[TD([[subQ4,-1.0]])],"derivedFrom":subQ3}),1.0]])]});}
            var Q11;
            {var subQ1=sQuery(id+"F2.wireOp",EDGE,"E9.10.2");Q11=makeQuery(id+"F2.imprint","IMPRINT",FACE,{"disambiguationData":[TD([[makeQuery(id+"F2.imprint","IMPRINT",EDGE,{"derivedFrom":subQ1}),-1.0]])]});}
            var Q12;
            {var subQ0=sQuery(id+"F2.wireOp",EDGE,"E16.8.0");var subQ1=sQuery(id+"F2.wireOp",EDGE,"E1");var subQ2=makeQuery(id+"F2.imprint","INTERSECT",VERTEX,{"derivedFrom":[subQ1,subQ0]});Q12=makeQuery(id+"F2.imprint","IMPRINT",FACE,{"disambiguationData":[TD([[makeQuery(id+"F2.imprint","IMPRINT",EDGE,{"disambiguationData":[TD([[subQ2,-1.0]])],"derivedFrom":subQ1}),1.0]])]});}
            var Q13;
            {var subQ0=sQuery(id+"F2.wireOp",EDGE,"E16.8.1");var subQ1=sQuery(id+"F2.wireOp",EDGE,"E9.8.1");var subQ2=makeQuery(id+"F2.imprint","INTERSECT",VERTEX,{"derivedFrom":[subQ1,subQ0]});Q13=makeQuery(id+"F2.imprint","IMPRINT",FACE,{"disambiguationData":[TD([[makeQuery(id+"F2.imprint","IMPRINT",EDGE,{"disambiguationData":[TD([[subQ2,-1.0]])],"derivedFrom":subQ1}),-1.0]])]});}
            var Q14;
            {var subQ1=sQuery(id+"F2.wireOp",EDGE,"E9.8.2");Q14=makeQuery(id+"F2.imprint","IMPRINT",FACE,{"disambiguationData":[TD([[makeQuery(id+"F2.imprint","IMPRINT",EDGE,{"derivedFrom":subQ1}),-1.0]])]});}
            var Q15;
            {var subQ1=sQuery(id+"F2.wireOp",EDGE,"E1");var subQ3=sQuery(id+"F2.wireOp",EDGE,"E16.8.0");var subQ4=makeQuery(id+"F2.imprint","INTERSECT",VERTEX,{"derivedFrom":[subQ1,subQ3]});Q15=makeQuery(id+"F2.imprint","IMPRINT",FACE,{"disambiguationData":[TD([[makeQuery(id+"F2.imprint","IMPRINT",EDGE,{"disambiguationData":[TD([[subQ4,-1.0]])],"derivedFrom":subQ3}),1.0]])]});}
            var Q16;
            {var subQ0=sQuery(id+"F2.wireOp",EDGE,"E16.7.0");var subQ1=sQuery(id+"F2.wireOp",EDGE,"E1");var subQ2=makeQuery(id+"F2.imprint","INTERSECT",VERTEX,{"derivedFrom":[subQ1,subQ0]});Q16=makeQuery(id+"F2.imprint","IMPRINT",FACE,{"disambiguationData":[TD([[makeQuery(id+"F2.imprint","IMPRINT",EDGE,{"disambiguationData":[TD([[subQ2,-1.0]])],"derivedFrom":subQ1}),1.0]])]});}
            var Q17;
            {var subQ0=sQuery(id+"F2.wireOp",EDGE,"E16.7.1");var subQ1=sQuery(id+"F2.wireOp",EDGE,"E9.7.1");var subQ2=makeQuery(id+"F2.imprint","INTERSECT",VERTEX,{"derivedFrom":[subQ1,subQ0]});Q17=makeQuery(id+"F2.imprint","IMPRINT",FACE,{"disambiguationData":[TD([[makeQuery(id+"F2.imprint","IMPRINT",EDGE,{"disambiguationData":[TD([[subQ2,-1.0]])],"derivedFrom":subQ1}),-1.0]])]});}
            var Q18;
            {var subQ1=sQuery(id+"F2.wireOp",EDGE,"E9.7.2");Q18=makeQuery(id+"F2.imprint","IMPRINT",FACE,{"disambiguationData":[TD([[makeQuery(id+"F2.imprint","IMPRINT",EDGE,{"derivedFrom":subQ1}),-1.0]])]});}
            var Q19;
            {var subQ1=sQuery(id+"F2.wireOp",EDGE,"E1");var subQ3=sQuery(id+"F2.wireOp",EDGE,"E16.7.0");var subQ4=makeQuery(id+"F2.imprint","INTERSECT",VERTEX,{"derivedFrom":[subQ1,subQ3]});Q19=makeQuery(id+"F2.imprint","IMPRINT",FACE,{"disambiguationData":[TD([[makeQuery(id+"F2.imprint","IMPRINT",EDGE,{"disambiguationData":[TD([[subQ4,-1.0]])],"derivedFrom":subQ3}),1.0]])]});}
            var Q20;
            {var subQ0=sQuery(id+"F2.wireOp",EDGE,"E16.6.1");var subQ1=sQuery(id+"F2.wireOp",EDGE,"E9.6.1");var subQ2=makeQuery(id+"F2.imprint","INTERSECT",VERTEX,{"derivedFrom":[subQ1,subQ0]});Q20=makeQuery(id+"F2.imprint","IMPRINT",FACE,{"disambiguationData":[TD([[makeQuery(id+"F2.imprint","IMPRINT",EDGE,{"disambiguationData":[TD([[subQ2,-1.0]])],"derivedFrom":subQ1}),-1.0]])]});}
            var Q21;
            {var subQ0=sQuery(id+"F2.wireOp",EDGE,"E16.6.0");var subQ1=sQuery(id+"F2.wireOp",EDGE,"E1");var subQ2=makeQuery(id+"F2.imprint","INTERSECT",VERTEX,{"derivedFrom":[subQ1,subQ0]});Q21=makeQuery(id+"F2.imprint","IMPRINT",FACE,{"disambiguationData":[TD([[makeQuery(id+"F2.imprint","IMPRINT",EDGE,{"disambiguationData":[TD([[subQ2,-1.0]])],"derivedFrom":subQ1}),1.0]])]});}
            var Q22;
            {var subQ1=sQuery(id+"F2.wireOp",EDGE,"E1");var subQ3=sQuery(id+"F2.wireOp",EDGE,"E16.6.0");var subQ4=makeQuery(id+"F2.imprint","INTERSECT",VERTEX,{"derivedFrom":[subQ1,subQ3]});Q22=makeQuery(id+"F2.imprint","IMPRINT",FACE,{"disambiguationData":[TD([[makeQuery(id+"F2.imprint","IMPRINT",EDGE,{"disambiguationData":[TD([[subQ4,-1.0]])],"derivedFrom":subQ3}),1.0]])]});}
            var Q23;
            {var subQ1=sQuery(id+"F2.wireOp",EDGE,"E9.6.2");Q23=makeQuery(id+"F2.imprint","IMPRINT",FACE,{"disambiguationData":[TD([[makeQuery(id+"F2.imprint","IMPRINT",EDGE,{"derivedFrom":subQ1}),-1.0]])]});}
            var Q24;
            {var subQ0=sQuery(id+"F2.wireOp",EDGE,"E16.5.1");var subQ1=sQuery(id+"F2.wireOp",EDGE,"E9.5.1");var subQ2=makeQuery(id+"F2.imprint","INTERSECT",VERTEX,{"derivedFrom":[subQ1,subQ0]});Q24=makeQuery(id+"F2.imprint","IMPRINT",FACE,{"disambiguationData":[TD([[makeQuery(id+"F2.imprint","IMPRINT",EDGE,{"disambiguationData":[TD([[subQ2,-1.0]])],"derivedFrom":subQ1}),-1.0]])]});}
            var Q25;
            {var subQ0=sQuery(id+"F2.wireOp",EDGE,"E16.5.0");var subQ1=sQuery(id+"F2.wireOp",EDGE,"E1");var subQ2=makeQuery(id+"F2.imprint","INTERSECT",VERTEX,{"derivedFrom":[subQ1,subQ0]});Q25=makeQuery(id+"F2.imprint","IMPRINT",FACE,{"disambiguationData":[TD([[makeQuery(id+"F2.imprint","IMPRINT",EDGE,{"disambiguationData":[TD([[subQ2,-1.0]])],"derivedFrom":subQ1}),1.0]])]});}
            var Q26;
            {var subQ1=sQuery(id+"F2.wireOp",EDGE,"E1");var subQ3=sQuery(id+"F2.wireOp",EDGE,"E16.5.0");var subQ4=makeQuery(id+"F2.imprint","INTERSECT",VERTEX,{"derivedFrom":[subQ1,subQ3]});Q26=makeQuery(id+"F2.imprint","IMPRINT",FACE,{"disambiguationData":[TD([[makeQuery(id+"F2.imprint","IMPRINT",EDGE,{"disambiguationData":[TD([[subQ4,-1.0]])],"derivedFrom":subQ3}),1.0]])]});}
            var Q27;
            {var subQ1=sQuery(id+"F2.wireOp",EDGE,"E9.5.2");Q27=makeQuery(id+"F2.imprint","IMPRINT",FACE,{"disambiguationData":[TD([[makeQuery(id+"F2.imprint","IMPRINT",EDGE,{"derivedFrom":subQ1}),-1.0]])]});}
            var Q28;
            {var subQ0=sQuery(id+"F2.wireOp",EDGE,"E16.4.1");var subQ1=sQuery(id+"F2.wireOp",EDGE,"E9.4.1");var subQ2=makeQuery(id+"F2.imprint","INTERSECT",VERTEX,{"derivedFrom":[subQ1,subQ0]});Q28=makeQuery(id+"F2.imprint","IMPRINT",FACE,{"disambiguationData":[TD([[makeQuery(id+"F2.imprint","IMPRINT",EDGE,{"disambiguationData":[TD([[subQ2,-1.0]])],"derivedFrom":subQ1}),-1.0]])]});}
            var Q29;
            {var subQ0=sQuery(id+"F2.wireOp",EDGE,"E16.4.0");var subQ1=sQuery(id+"F2.wireOp",EDGE,"E1");var subQ2=makeQuery(id+"F2.imprint","INTERSECT",VERTEX,{"derivedFrom":[subQ1,subQ0]});Q29=makeQuery(id+"F2.imprint","IMPRINT",FACE,{"disambiguationData":[TD([[makeQuery(id+"F2.imprint","IMPRINT",EDGE,{"disambiguationData":[TD([[subQ2,-1.0]])],"derivedFrom":subQ1}),1.0]])]});}
            var Q30;
            {var subQ1=sQuery(id+"F2.wireOp",EDGE,"E9.4.2");Q30=makeQuery(id+"F2.imprint","IMPRINT",FACE,{"disambiguationData":[TD([[makeQuery(id+"F2.imprint","IMPRINT",EDGE,{"derivedFrom":subQ1}),-1.0]])]});}
            var Q31;
            {var subQ1=sQuery(id+"F2.wireOp",EDGE,"E1");var subQ3=sQuery(id+"F2.wireOp",EDGE,"E16.4.0");var subQ4=makeQuery(id+"F2.imprint","INTERSECT",VERTEX,{"derivedFrom":[subQ1,subQ3]});Q31=makeQuery(id+"F2.imprint","IMPRINT",FACE,{"disambiguationData":[TD([[makeQuery(id+"F2.imprint","IMPRINT",EDGE,{"disambiguationData":[TD([[subQ4,-1.0]])],"derivedFrom":subQ3}),1.0]])]});}
            var Q32;
            {var subQ0=sQuery(id+"F2.wireOp",EDGE,"E16.2.1");var subQ1=sQuery(id+"F2.wireOp",EDGE,"E9.2.1");var subQ2=makeQuery(id+"F2.imprint","INTERSECT",VERTEX,{"derivedFrom":[subQ1,subQ0]});Q32=makeQuery(id+"F2.imprint","IMPRINT",FACE,{"disambiguationData":[TD([[makeQuery(id+"F2.imprint","IMPRINT",EDGE,{"disambiguationData":[TD([[subQ2,-1.0]])],"derivedFrom":subQ1}),-1.0]])]});}
            var Q33;
            {var subQ1=sQuery(id+"F2.wireOp",EDGE,"E9.2.2");Q33=makeQuery(id+"F2.imprint","IMPRINT",FACE,{"disambiguationData":[TD([[makeQuery(id+"F2.imprint","IMPRINT",EDGE,{"derivedFrom":subQ1}),-1.0]])]});}
            var Q34;
            {var subQ1=sQuery(id+"F2.wireOp",EDGE,"E1");var subQ3=sQuery(id+"F2.wireOp",EDGE,"E16.2.0");var subQ4=makeQuery(id+"F2.imprint","INTERSECT",VERTEX,{"derivedFrom":[subQ1,subQ3]});Q34=makeQuery(id+"F2.imprint","IMPRINT",FACE,{"disambiguationData":[TD([[makeQuery(id+"F2.imprint","IMPRINT",EDGE,{"disambiguationData":[TD([[subQ4,-1.0]])],"derivedFrom":subQ3}),1.0]])]});}
            var Q35;
            {var subQ0=sQuery(id+"F2.wireOp",EDGE,"E16.2.0");var subQ1=sQuery(id+"F2.wireOp",EDGE,"E1");var subQ2=makeQuery(id+"F2.imprint","INTERSECT",VERTEX,{"derivedFrom":[subQ1,subQ0]});Q35=makeQuery(id+"F2.imprint","IMPRINT",FACE,{"disambiguationData":[TD([[makeQuery(id+"F2.imprint","IMPRINT",EDGE,{"disambiguationData":[TD([[subQ2,-1.0]])],"derivedFrom":subQ1}),1.0]])]});}
            var Q36;
            {var subQ0=sQuery(id+"F2.wireOp",EDGE,"E16.1.0");var subQ1=sQuery(id+"F2.wireOp",EDGE,"E1");var subQ2=makeQuery(id+"F2.imprint","INTERSECT",VERTEX,{"derivedFrom":[subQ1,subQ0]});Q36=makeQuery(id+"F2.imprint","IMPRINT",FACE,{"disambiguationData":[TD([[makeQuery(id+"F2.imprint","IMPRINT",EDGE,{"disambiguationData":[TD([[subQ2,-1.0]])],"derivedFrom":subQ1}),1.0]])]});}
            var Q37;
            {var subQ0=sQuery(id+"F2.wireOp",EDGE,"E16.1.1");var subQ1=sQuery(id+"F2.wireOp",EDGE,"E9.1.1");var subQ2=makeQuery(id+"F2.imprint","INTERSECT",VERTEX,{"derivedFrom":[subQ1,subQ0]});Q37=makeQuery(id+"F2.imprint","IMPRINT",FACE,{"disambiguationData":[TD([[makeQuery(id+"F2.imprint","IMPRINT",EDGE,{"disambiguationData":[TD([[subQ2,-1.0]])],"derivedFrom":subQ1}),-1.0]])]});}
            var Q38;
            {var subQ1=sQuery(id+"F2.wireOp",EDGE,"E9.1.2");Q38=makeQuery(id+"F2.imprint","IMPRINT",FACE,{"disambiguationData":[TD([[makeQuery(id+"F2.imprint","IMPRINT",EDGE,{"derivedFrom":subQ1}),-1.0]])]});}
            var Q39;
            {var subQ1=sQuery(id+"F2.wireOp",EDGE,"E1");var subQ3=sQuery(id+"F2.wireOp",EDGE,"E16.1.0");var subQ4=makeQuery(id+"F2.imprint","INTERSECT",VERTEX,{"derivedFrom":[subQ1,subQ3]});Q39=makeQuery(id+"F2.imprint","IMPRINT",FACE,{"disambiguationData":[TD([[makeQuery(id+"F2.imprint","IMPRINT",EDGE,{"disambiguationData":[TD([[subQ4,-1.0]])],"derivedFrom":subQ3}),1.0]])]});}
            extrude(context, id + "F9", {"entities" : qUnion([Q0, Q1, Q2, Q3, Q4, Q5, Q6, Q7, Q8, Q9, Q10, Q11, Q12, Q13, Q14, Q15, Q16, Q17, Q18, Q19, Q20, Q21, Q22, Q23, Q24, Q25, Q26, Q27, Q28, Q29, Q30, Q31, Q32, Q33, Q34, Q35, Q36, Q37, Q38, Q39]), "operationType" : NewBodyOperationType.ADD, "depth" : 6 * mm, "offsetDistance" : 25 * mm});
        }
    });
